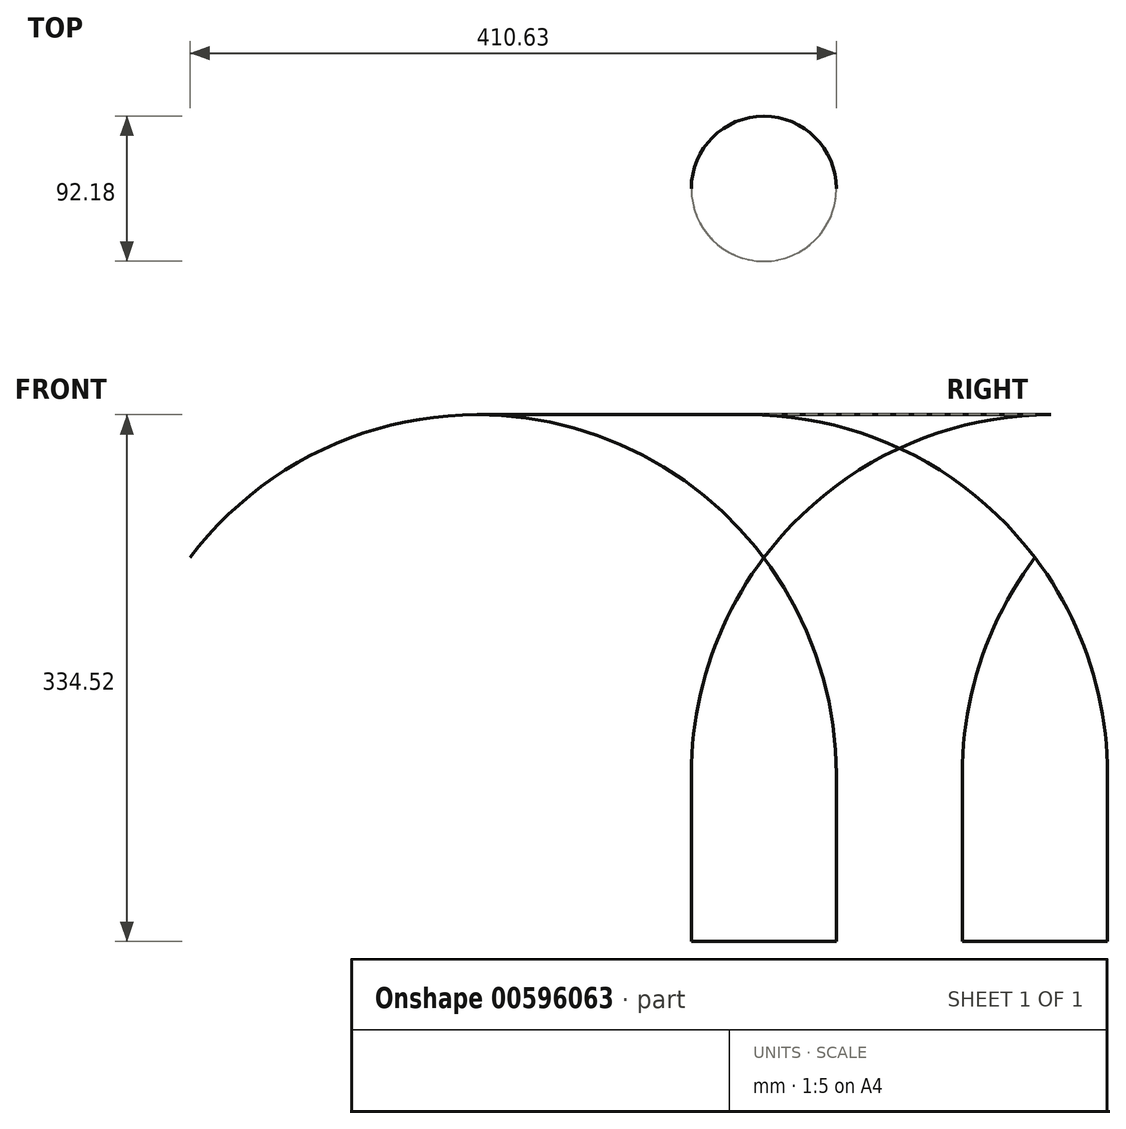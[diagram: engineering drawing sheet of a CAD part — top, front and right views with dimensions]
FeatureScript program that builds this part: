
annotation { "Feature Type Name" : "Feature", "Feature Type Description" : "" }
export const myFeature = defineFeature(function(context is Context, id is Id, definition is map)
    precondition{}
    {
        {
            var Q0;
            Q0=qCreatedBy(makeId("Right.planeOp"),FACE);
            var sketch = newSketch(context, id + "F0", { "sketchPlane" : qUnion([Q0])});
            skLineSegment(sketch, "E0.bottom", {"start": v(0, 0) * mm, "end": v(46.09, 0) * mm});
            skLineSegment(sketch, "E0.left", {"start": v(0, 0) * mm, "end": v(0, 106.17) * mm});
            skLineSegment(sketch, "E0.right", {"start": v(46.09, 0) * mm, "end": v(46.09, 106.17) * mm});
            skLineSegment(sketch, "E1", {"start": v(0, 106.17) * mm, "end": v(0, 243.73) * mm});
            skArc(sketch, "E2", {"start": v(46.09, 106.17) * mm, "mid": v(34.26, 178.7) * mm, "end": v(0, 243.73) * mm});
            skSolve(sketch);
        }
        {
            var Q0;
            Q0=makeQuery(id+"F0.imprint","IMPRINT",FACE,{"disambiguationData":[TD([[makeQuery(id+"F0.imprint","IMPRINT",EDGE,{"derivedFrom":sQuery(id+"F0.wireOp",EDGE,"E0.bottom")}),1.0]])]});
            var Q1;
            Q1=sQuery(id+"F0.wireOp",EDGE,"E0.left");
            revolve(context, id + "F1", {"entities" : qUnion([Q0]), "axis" : qUnion([Q1]), "revolveType" : RevolveType.FULL});
        }
    });
